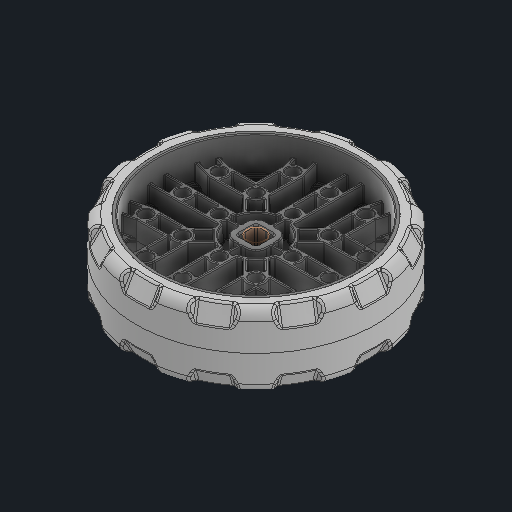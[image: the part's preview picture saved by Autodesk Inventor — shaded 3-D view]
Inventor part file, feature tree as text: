
AUTODESK INVENTOR PART (.ipt)
format: ipt  version: 2024 (Build 280153000, 153)  size: 12,623,872 bytes
history: native  units: in
note: dims shown in document units (in); Inventor stores cm internally (conversion verified against a paired STEP export)
features: other x6, sketch x1
ambient origin geometry x8: Origin, YZ Plane, XZ Plane, XY Plane, X Axis, Y Axis, Z Axis, Center Point
bodies: Solid1 (feature_tree), Solid2 (feature_tree)
feature tree (7):
  other  "3.25 Traction Antistatic.ipt"
  other  "Solid1::3.25 Traction Antistatic.ipt"
  other  "Solid2::3.25 Traction Antistatic.ipt"
  other  "TaggingFeature1"
  sketch  "Sketch1"  dims[d0=0.3937in]
  other  "Srf1"
  other  "Srf1::Derived"
